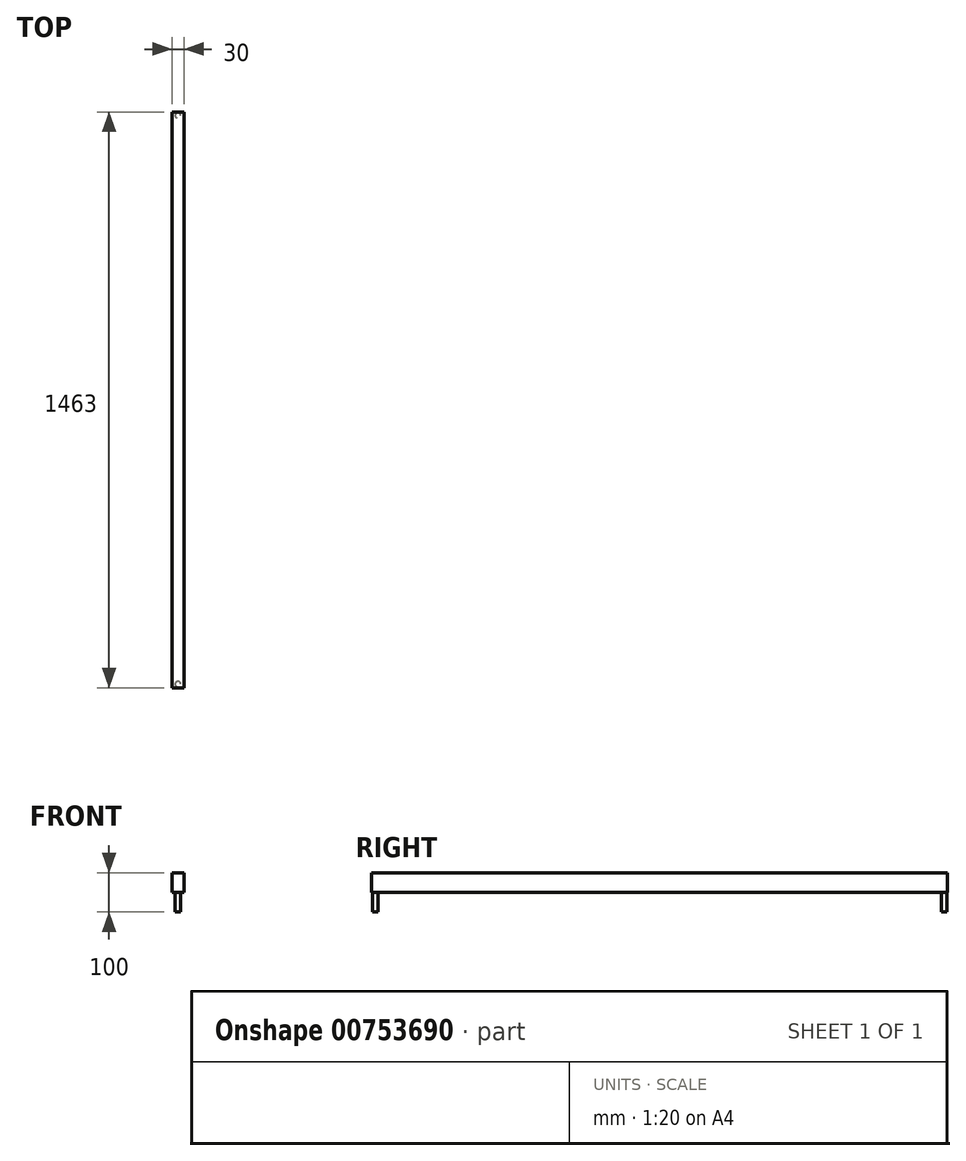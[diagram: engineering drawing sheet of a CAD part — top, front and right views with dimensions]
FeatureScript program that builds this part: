
annotation { "Feature Type Name" : "Feature", "Feature Type Description" : "" }
export const myFeature = defineFeature(function(context is Context, id is Id, definition is map)
    precondition{}
    {
        {
            var Q0;
            Q0=qCreatedBy(makeId("Right.planeOp"),FACE);
            var sketch = newSketch(context, id + "F0", { "sketchPlane" : qUnion([Q0])});
            skLineSegment(sketch, "E0.bottom", {"start": v(731.5, -25) * mm, "end": v(-731.5, -25) * mm});
            skLineSegment(sketch, "E0.top", {"start": v(731.5, 25) * mm, "end": v(-731.5, 25) * mm});
            skLineSegment(sketch, "E0.left", {"start": v(731.5, -25) * mm, "end": v(731.5, 25) * mm});
            skLineSegment(sketch, "E0.right", {"start": v(-731.5, -25) * mm, "end": v(-731.5, 25) * mm});
            skPoint(sketch, "E0.middle", {"position": v(0, 0) * mm});
            skSolve(sketch);
        }
        {
            var Q0;
            Q0=qSketchRegion(id+"F0",true);
            extrude(context, id + "F1", {"entities" : qUnion([Q0]), "depth" : 15 * mm, "offsetDistance" : 25 * mm, "hasSecondDirection" : true, "secondDirectionOppositeDirection" : true, "secondDirectionDepth" : 15 * mm});
        }
        {
            var Q0;
            Q0=makeQuery(id+"F1.opExtrude","SWEPT_FACE",FACE,{"disambiguationData":[OSD([sQuery(id+"F0.wireOp",EDGE,"E0.bottom")])]});
            var sketch = newSketch(context, id + "F2", { "sketchPlane" : qUnion([Q0])});
            skLineSegment(sketch, "E1.0", {"start": v(15, 731.5) * mm, "end": v(-15, 731.5) * mm});
            skLineSegment(sketch, "E2", {"start": v(0, 731.5) * mm, "end": v(0, 729.5) * mm});
            skLineSegment(sketch, "E3", {"start": v(0, 729.5) * mm, "end": v(0, 722.5) * mm});
            skCircle(sketch, "E4", {"center": v(0, 722.5) * mm, "radius": 7 * mm});
            skSolve(sketch);
        }
        {
            var Q0;
            Q0=qSketchRegion(id+"F2",true);
            extrude(context, id + "F3", {"entities" : qUnion([Q0]), "operationType" : NewBodyOperationType.ADD, "depth" : 50 * mm, "offsetDistance" : 25 * mm});
        }
        {
            var Q0;
            Q0=makeQuery(id+"F1.opExtrude","SWEPT_FACE",FACE,{"disambiguationData":[OSD([sQuery(id+"F0.wireOp",EDGE,"E0.bottom")])]});
            var sketch = newSketch(context, id + "F4", { "sketchPlane" : qUnion([Q0])});
            skLineSegment(sketch, "E5.0", {"start": v(15, -731.5) * mm, "end": v(-15, -731.5) * mm});
            skLineSegment(sketch, "E6", {"start": v(0, -731.5) * mm, "end": v(0, -729.5) * mm});
            skLineSegment(sketch, "E7", {"start": v(0, -729.5) * mm, "end": v(0, -722.5) * mm});
            skCircle(sketch, "E8", {"center": v(0, -722.5) * mm, "radius": 7 * mm});
            skSolve(sketch);
        }
        {
            var Q0;
            Q0=qSketchRegion(id+"F4",true);
            extrude(context, id + "F5", {"entities" : qUnion([Q0]), "operationType" : NewBodyOperationType.ADD, "depth" : 50 * mm, "offsetDistance" : 25 * mm});
        }
    });
